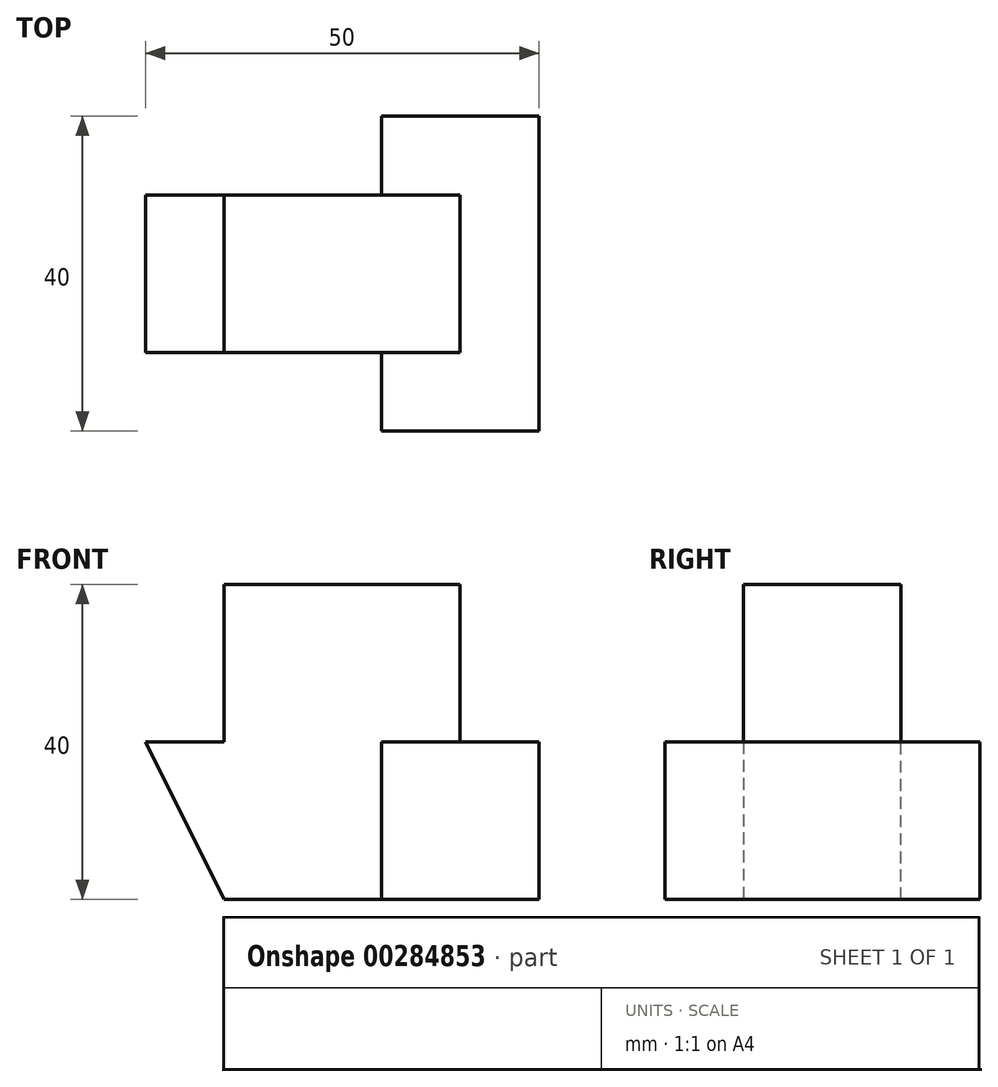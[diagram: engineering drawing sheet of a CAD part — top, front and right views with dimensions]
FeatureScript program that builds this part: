
annotation { "Feature Type Name" : "Feature", "Feature Type Description" : "" }
export const myFeature = defineFeature(function(context is Context, id is Id, definition is map)
    precondition{}
    {
        {
            var Q0;
            Q0=qCreatedBy(makeId("Front.planeOp"),FACE);
            var sketch = newSketch(context, id + "F0", { "sketchPlane" : qUnion([Q0])});
            skLineSegment(sketch, "E0.bottom", {"start": v(0, 0) * mm, "end": v(50, 0) * mm});
            skLineSegment(sketch, "E0.top", {"start": v(0, 40) * mm, "end": v(50, 40) * mm});
            skLineSegment(sketch, "E0.left", {"start": v(0, 0) * mm, "end": v(0, 40) * mm});
            skLineSegment(sketch, "E0.right", {"start": v(50, 0) * mm, "end": v(50, 40) * mm});
            skSolve(sketch);
        }
        {
            var Q0;
            Q0=makeQuery(id+"F0.imprint","IMPRINT",FACE,{"disambiguationData":[TD([[makeQuery(id+"F0.imprint","IMPRINT",EDGE,{"derivedFrom":sQuery(id+"F0.wireOp",EDGE,"E0.bottom")}),1.0]])]});
            extrude(context, id + "F1", {"entities" : qUnion([Q0]), "depth" : 40 * mm});
        }
        {
            var Q0;
            Q0=makeQuery(id+"F1.opExtrude","SWEPT_FACE",FACE,{"disambiguationData":[OSD([sQuery(id+"F0.wireOp",EDGE,"E0.left")])]});
            var sketch = newSketch(context, id + "F2", { "sketchPlane" : qUnion([Q0])});
            skLineSegment(sketch, "E1", {"start": v(0, 20) * mm, "end": v(40, 20) * mm});
            skLineSegment(sketch, "E2", {"start": v(30, 40) * mm, "end": v(30, 20) * mm});
            skLineSegment(sketch, "E3", {"start": v(10, 40) * mm, "end": v(10, 20) * mm});
            skLineSegment(sketch, "E4.0", {"start": v(40, 40) * mm, "end": v(0, 40) * mm});
            skLineSegment(sketch, "E5.0.1", {"start": v(40, 40) * mm, "end": v(40, 20) * mm});
            skLineSegment(sketch, "E5.0.3", {"start": v(40, 20) * mm, "end": v(40, 40) * mm});
            skLineSegment(sketch, "E6.0.1", {"start": v(0, 40) * mm, "end": v(0, 20) * mm});
            skLineSegment(sketch, "E6.0.3", {"start": v(0, 0) * mm, "end": v(0, 40) * mm});
            skPoint(sketch, "E7.orphan", {"position": v(40, 0) * mm});
            skPoint(sketch, "E8.orphan", {"position": v(0, 0) * mm});
            skSolve(sketch);
        }
        {
            var Q0;
            {var subQ3=sQuery(id+"F2.wireOp",EDGE,"E3");Q0=makeQuery(id+"F2.imprint","IMPRINT",FACE,{"disambiguationData":[TD([[makeQuery(id+"F2.imprint","IMPRINT",EDGE,{"derivedFrom":subQ3}),-1.0]])]});}
            var Q1;
            {var subQ2=sQuery(id+"F2.wireOp",EDGE,"E2");Q1=makeQuery(id+"F2.imprint","IMPRINT",FACE,{"disambiguationData":[TD([[makeQuery(id+"F2.imprint","IMPRINT",EDGE,{"derivedFrom":subQ2}),1.0]])]});}
            extrude(context, id + "F3", {"entities" : qUnion([Q0, Q1]), "operationType" : NewBodyOperationType.REMOVE, "endBound" : BoundingType.THROUGH_ALL, "oppositeDirection" : true, "depth" : 30 * mm});
        }
        {
            var Q0;
            {var subQ0=sQuery(id+"F2.wireOp",EDGE,"E1");Q0=makeQuery(id+"F3.boolean.opBoolean","COPY",FACE,{"derivedFrom":makeQuery(id+"F3.opExtrude","SWEPT_FACE",FACE,{"disambiguationData":[OSD([subQ0]),TDD([makeQuery(id+"F2.imprint","IMPRINT",EDGE,{"disambiguationData":[TD([[makeQuery(id+"F2.imprint","INTERSECT",VERTEX,{"derivedFrom":[subQ0,sQuery(id+"F2.wireOp",EDGE,"E6.0.3")]}),-1.0]])],"derivedFrom":subQ0})])]})});}
            var sketch = newSketch(context, id + "F4", { "sketchPlane" : qUnion([Q0])});
            skLineSegment(sketch, "E9.0", {"start": v(50, 0) * mm, "end": v(30, 0) * mm});
            skLineSegment(sketch, "E10.0", {"start": v(50, -10) * mm, "end": v(30, -10) * mm});
            skLineSegment(sketch, "E11.0", {"start": v(50, -30) * mm, "end": v(30, -30) * mm});
            skLineSegment(sketch, "E12.0", {"start": v(50, -40) * mm, "end": v(30, -40) * mm});
            skLineSegment(sketch, "E13", {"start": v(30, 0) * mm, "end": v(30, -10) * mm});
            skLineSegment(sketch, "E14", {"start": v(30, -30) * mm, "end": v(30, -40) * mm});
            skLineSegment(sketch, "E15.0", {"start": v(50, -30) * mm, "end": v(50, -40) * mm});
            skLineSegment(sketch, "E16.0", {"start": v(50, 0) * mm, "end": v(50, -10) * mm});
            skPoint(sketch, "E17.orphan", {"position": v(0, -10) * mm});
            skPoint(sketch, "E18.orphan", {"position": v(0, -30) * mm});
            skPoint(sketch, "E19.orphan", {"position": v(0, -40) * mm});
            skPoint(sketch, "E20.orphan", {"position": v(0, 0) * mm});
            skLineSegment(sketch, "E21.0", {"start": v(50, 0) * mm, "end": v(0, 0) * mm});
            skLineSegment(sketch, "E22.0", {"start": v(50, -10) * mm, "end": v(0, -10) * mm});
            skLineSegment(sketch, "E23.0", {"start": v(0, 0) * mm, "end": v(0, -10) * mm});
            skLineSegment(sketch, "E24.0", {"start": v(0, -30) * mm, "end": v(0, -40) * mm});
            skLineSegment(sketch, "E25.0", {"start": v(50, -40) * mm, "end": v(0, -40) * mm});
            skLineSegment(sketch, "E26.0", {"start": v(50, -30) * mm, "end": v(0, -30) * mm});
            skSolve(sketch);
        }
        {
            var Q0;
            {var subQ0=sQuery(id+"F4.wireOp",EDGE,"E13");Q0=makeQuery(id+"F4.imprint","IMPRINT",FACE,{"disambiguationData":[TD([[makeQuery(id+"F4.imprint","IMPRINT",EDGE,{"derivedFrom":subQ0}),-1.0]])]});}
            var Q1;
            {var subQ0=sQuery(id+"F4.wireOp",EDGE,"E14");Q1=makeQuery(id+"F4.imprint","IMPRINT",FACE,{"disambiguationData":[TD([[makeQuery(id+"F4.imprint","IMPRINT",EDGE,{"derivedFrom":subQ0}),-1.0]])]});}
            extrude(context, id + "F5", {"entities" : qUnion([Q0, Q1]), "operationType" : NewBodyOperationType.REMOVE, "endBound" : BoundingType.THROUGH_ALL, "oppositeDirection" : true, "depth" : 25 * mm});
        }
        {
            var Q0;
            Q0=makeQuery(id+"F1.opExtrude","SWEPT_FACE",FACE,{"disambiguationData":[OSD([sQuery(id+"F0.wireOp",EDGE,"E0.top")])]});
            var sketch = newSketch(context, id + "F6", { "sketchPlane" : qUnion([Q0])});
            skLineSegment(sketch, "E27", {"start": v(40, -10) * mm, "end": v(40, -30) * mm});
            skLineSegment(sketch, "E28.0", {"start": v(50, -10) * mm, "end": v(0, -10) * mm});
            skLineSegment(sketch, "E29.0", {"start": v(50, -30) * mm, "end": v(50, -10) * mm});
            skLineSegment(sketch, "E30.0", {"start": v(50, -30) * mm, "end": v(0, -30) * mm});
            skSolve(sketch);
        }
        {
            var Q0;
            Q0=qSketchRegion(id+"F6",true);
            var Q1;
            {var subQ0=sQuery(id+"F2.wireOp",EDGE,"E1");Q1=makeQuery(id+"F3.boolean.opBoolean","COPY",FACE,{"derivedFrom":makeQuery(id+"F3.opExtrude","SWEPT_FACE",FACE,{"disambiguationData":[OSD([subQ0]),TDD([makeQuery(id+"F2.imprint","IMPRINT",EDGE,{"disambiguationData":[TD([[makeQuery(id+"F2.imprint","INTERSECT",VERTEX,{"derivedFrom":[subQ0,sQuery(id+"F2.wireOp",EDGE,"E6.0.3")]}),-1.0]])],"derivedFrom":subQ0})])]})});}
            extrude(context, id + "F7", {"entities" : qUnion([Q0]), "operationType" : NewBodyOperationType.REMOVE, "endBound" : BoundingType.UP_TO_SURFACE, "oppositeDirection" : true, "endBoundEntityFace" : qUnion([Q1]), "depth" : 25 * mm});
        }
        {
            var Q0;
            Q0=makeQuery(id+"F5.boolean.opBoolean","MERGE",FACE,{"derivedFrom":[makeQuery(id+"F3.boolean.opBoolean","COPY",FACE,{"derivedFrom":makeQuery(id+"F3.opExtrude","SWEPT_FACE",FACE,{"disambiguationData":[OSD([sQuery(id+"F2.wireOp",EDGE,"E2")])]})}),makeQuery(id+"F5.opExtrude","SWEPT_FACE",FACE,{"disambiguationData":[OSD([sQuery(id+"F4.wireOp",EDGE,"E26.0")])]})]});
            var sketch = newSketch(context, id + "F8", { "sketchPlane" : qUnion([Q0])});
            skLineSegment(sketch, "E31.bottom", {"start": v(0, 40) * mm, "end": v(10, 40) * mm});
            skLineSegment(sketch, "E31.top", {"start": v(0, 20) * mm, "end": v(10, 20) * mm});
            skLineSegment(sketch, "E31.left", {"start": v(0, 40) * mm, "end": v(0, 20) * mm});
            skLineSegment(sketch, "E31.right", {"start": v(10, 40) * mm, "end": v(10, 20) * mm});
            skLineSegment(sketch, "E32", {"start": v(0, 20) * mm, "end": v(10, 0) * mm});
            skLineSegment(sketch, "E33", {"start": v(10, 0) * mm, "end": v(0, 0) * mm});
            skLineSegment(sketch, "E34", {"start": v(0, 0) * mm, "end": v(0, 20) * mm});
            skSolve(sketch);
        }
        {
            var Q0;
            Q0=qSketchRegion(id+"F8",true);
            extrude(context, id + "F9", {"entities" : qUnion([Q0]), "operationType" : NewBodyOperationType.REMOVE, "endBound" : BoundingType.THROUGH_ALL, "oppositeDirection" : true, "depth" : 25 * mm});
        }
    });
